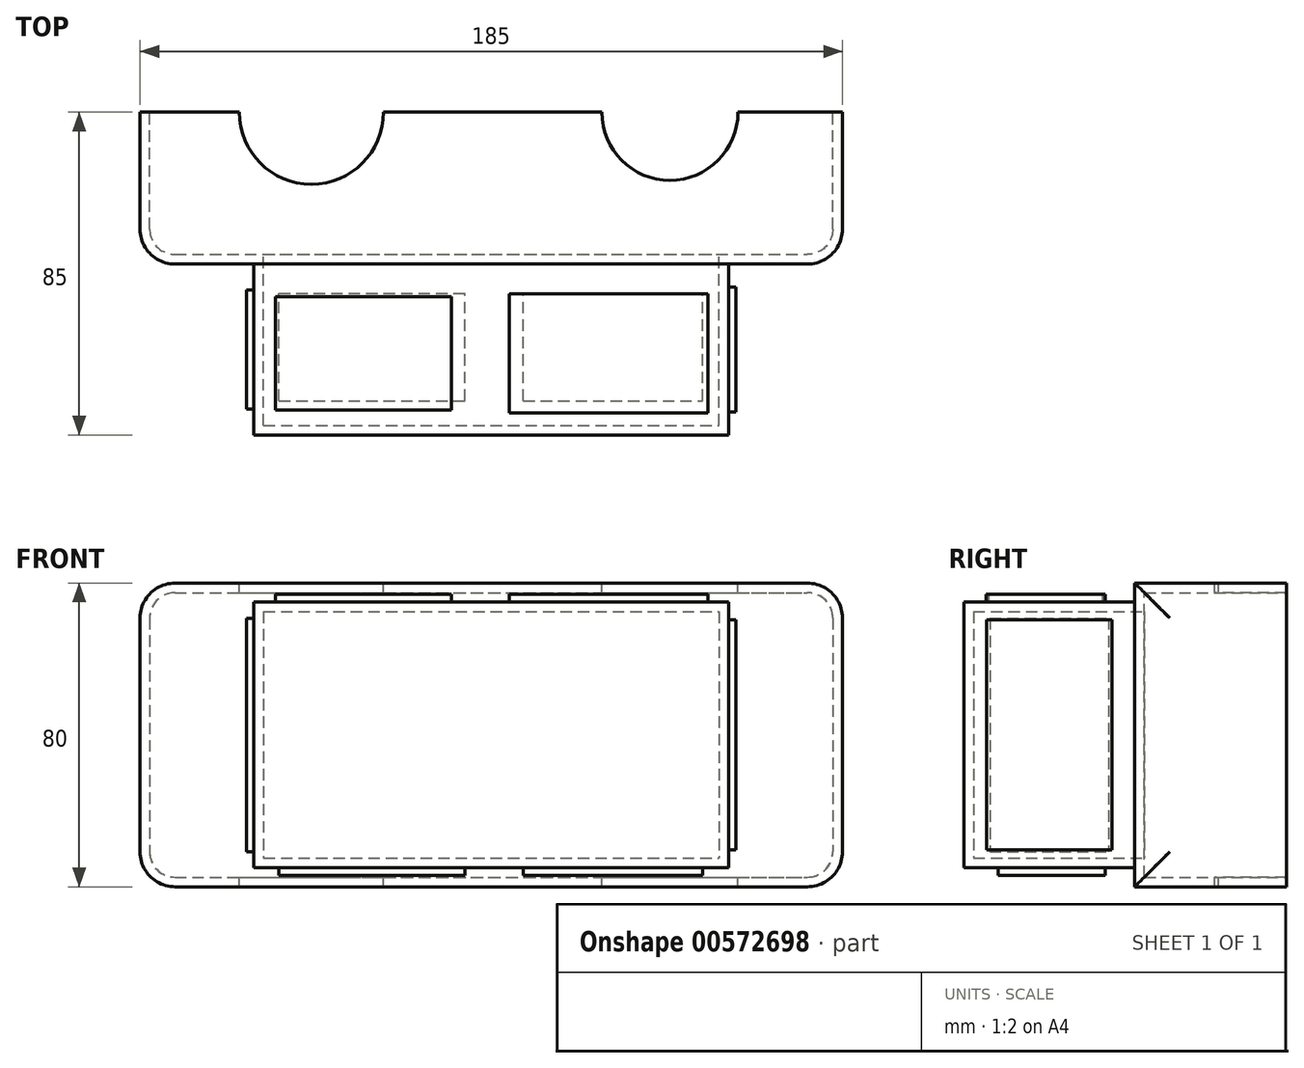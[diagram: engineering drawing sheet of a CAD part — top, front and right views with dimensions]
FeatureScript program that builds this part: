
annotation { "Feature Type Name" : "Feature", "Feature Type Description" : "" }
export const myFeature = defineFeature(function(context is Context, id is Id, definition is map)
    precondition{}
    {
        {
            var Q0;
            Q0=qCreatedBy(makeId("Front.planeOp"),FACE);
            var sketch = newSketch(context, id + "F0", { "sketchPlane" : qUnion([Q0])});
            skLineSegment(sketch, "E0.bottom", {"start": v(-92.5, 40) * mm, "end": v(92.5, 40) * mm});
            skLineSegment(sketch, "E0.top", {"start": v(-92.5, -40) * mm, "end": v(92.5, -40) * mm});
            skLineSegment(sketch, "E0.left", {"start": v(-92.5, 40) * mm, "end": v(-92.5, -40) * mm});
            skLineSegment(sketch, "E0.right", {"start": v(92.5, 40) * mm, "end": v(92.5, -40) * mm});
            skPoint(sketch, "E0.middle", {"position": v(0, 0) * mm});
            skSolve(sketch);
        }
        {
            var Q0;
            Q0=makeQuery(id+"F0.imprint","IMPRINT",FACE,{"disambiguationData":[TD([[makeQuery(id+"F0.imprint","IMPRINT",EDGE,{"derivedFrom":sQuery(id+"F0.wireOp",EDGE,"E0.bottom")}),-1.0]])]});
            extrude(context, id + "F1", {"entities" : qUnion([Q0]), "depth" : 40 * mm, "offsetDistance" : 25.4 * mm});
        }
        {
            var Q0;
            Q0=makeQuery(id+"F1.opExtrude","CAP_FACE",FACE,{"disambiguationData":[OSD([sQuery(id+"F0.wireOp",EDGE,"E0.bottom"),sQuery(id+"F0.wireOp",EDGE,"E0.top"),sQuery(id+"F0.wireOp",EDGE,"E0.left"),sQuery(id+"F0.wireOp",EDGE,"E0.right")])],"isStart":false});
            var sketch = newSketch(context, id + "F2", { "sketchPlane" : qUnion([Q0])});
            skLineSegment(sketch, "E1.bottom", {"start": v(-62.5, 35) * mm, "end": v(62.5, 35) * mm});
            skLineSegment(sketch, "E1.top", {"start": v(-62.5, -35) * mm, "end": v(62.5, -35) * mm});
            skLineSegment(sketch, "E1.left", {"start": v(-62.5, 35) * mm, "end": v(-62.5, -35) * mm});
            skLineSegment(sketch, "E1.right", {"start": v(62.5, 35) * mm, "end": v(62.5, -35) * mm});
            skPoint(sketch, "E1.middle", {"position": v(0, 0) * mm});
            skSolve(sketch);
        }
        {
            var Q0;
            Q0=makeQuery(id+"F2.imprint","IMPRINT",FACE,{"disambiguationData":[TD([[makeQuery(id+"F2.imprint","IMPRINT",EDGE,{"derivedFrom":sQuery(id+"F2.wireOp",EDGE,"E1.bottom")}),-1.0]])]});
            extrude(context, id + "F3", {"entities" : qUnion([Q0]), "operationType" : NewBodyOperationType.ADD, "depth" : 45 * mm, "offsetDistance" : 25.4 * mm});
        }
        {
            var Q0;
            Q0=makeQuery(id+"F1.opExtrude","CAP_EDGE",EDGE,{"disambiguationData":[OSD([sQuery(id+"F0.wireOp",EDGE,"E0.left")])],"isStart":false});
            var Q1;
            Q1=makeQuery(id+"F1.opExtrude","CAP_EDGE",EDGE,{"disambiguationData":[OSD([sQuery(id+"F0.wireOp",EDGE,"E0.right")])],"isStart":false});
            var Q2;
            Q2=makeQuery(id+"F1.opExtrude","SWEPT_EDGE",EDGE,{"disambiguationData":[OSD([sQuery(id+"F0.wireOp",EDGE,"E0.bottom"),sQuery(id+"F0.wireOp",EDGE,"E0.right")])]});
            var Q3;
            Q3=makeQuery(id+"F1.opExtrude","SWEPT_EDGE",EDGE,{"disambiguationData":[OSD([sQuery(id+"F0.wireOp",EDGE,"E0.top"),sQuery(id+"F0.wireOp",EDGE,"E0.right")])]});
            var Q4;
            Q4=makeQuery(id+"F1.opExtrude","SWEPT_EDGE",EDGE,{"disambiguationData":[OSD([sQuery(id+"F0.wireOp",EDGE,"E0.top"),sQuery(id+"F0.wireOp",EDGE,"E0.left")])]});
            var Q5;
            Q5=makeQuery(id+"F1.opExtrude","SWEPT_EDGE",EDGE,{"disambiguationData":[OSD([sQuery(id+"F0.wireOp",EDGE,"E0.bottom"),sQuery(id+"F0.wireOp",EDGE,"E0.left")])]});
            fillet(context, id + "F4", {"entities" : qUnion([Q0, Q1, Q2, Q3, Q4, Q5]), "radius" : 9.2 * mm, "tangentPropagation" : true, "allowEdgeOverflow" : false});
        }
        {
            var Q0;
            Q0=makeQuery(id+"F1.opExtrude","CAP_FACE",FACE,{"disambiguationData":[OSD([sQuery(id+"F0.wireOp",EDGE,"E0.bottom"),sQuery(id+"F0.wireOp",EDGE,"E0.top"),sQuery(id+"F0.wireOp",EDGE,"E0.left"),sQuery(id+"F0.wireOp",EDGE,"E0.right")])],"isStart":true});
            shell(context, id + "F5", {"entities" : qUnion([Q0]), "thickness" : 2.54 * mm});
        }
        {
            var Q0;
            Q0=makeQuery(id+"F1.opExtrude","SWEPT_FACE",FACE,{"disambiguationData":[OSD([sQuery(id+"F0.wireOp",EDGE,"E0.bottom")])]});
            var sketch = newSketch(context, id + "F6", { "sketchPlane" : qUnion([Q0])});
            skCircle(sketch, "E2", {"center": v(-47.36, 0) * mm, "radius": 18.99 * mm});
            skCircle(sketch, "E3", {"center": v(47.06, 0) * mm, "radius": 17.94 * mm});
            skSolve(sketch);
        }
        {
            var Q0;
            {var subQ0=sQuery(id+"F6.wireOp",EDGE,"E2");var subQ1=makeQuery(id+"F1.opExtrude","CAP_EDGE",EDGE,{"disambiguationData":[OSD([sQuery(id+"F0.wireOp",EDGE,"E0.bottom")])],"isStart":true});var subQ2=makeQuery(id+"F6.imprint","INTERSECT",VERTEX,{"disambiguationData":[OD(0.0)],"derivedFrom":[subQ1,subQ0]});Q0=makeQuery(id+"F6.imprint","IMPRINT",FACE,{"disambiguationData":[TD([[makeQuery(id+"F6.imprint","IMPRINT",EDGE,{"disambiguationData":[TD([[subQ2,-1.0]])],"derivedFrom":subQ0}),1.0]])]});}
            var Q1;
            {var subQ0=sQuery(id+"F6.wireOp",EDGE,"E3");var subQ1=makeQuery(id+"F1.opExtrude","CAP_EDGE",EDGE,{"disambiguationData":[OSD([sQuery(id+"F0.wireOp",EDGE,"E0.bottom")])],"isStart":true});var subQ2=makeQuery(id+"F6.imprint","INTERSECT",VERTEX,{"disambiguationData":[OD(0.0)],"derivedFrom":[subQ1,subQ0]});Q1=makeQuery(id+"F6.imprint","IMPRINT",FACE,{"disambiguationData":[TD([[makeQuery(id+"F6.imprint","IMPRINT",EDGE,{"disambiguationData":[TD([[subQ2,1.0]])],"derivedFrom":subQ0}),1.0]])]});}
            extrude(context, id + "F7", {"entities" : qUnion([Q0, Q1]), "operationType" : NewBodyOperationType.REMOVE, "oppositeDirection" : true, "depth" : 112.6 * mm, "offsetDistance" : 25 * mm});
        }
        {
            var Q0;
            Q0=makeQuery(id+"F3.opExtrude","SWEPT_FACE",FACE,{"disambiguationData":[OSD([sQuery(id+"F2.wireOp",EDGE,"E1.top")])]});
            var sketch = newSketch(context, id + "F8", { "sketchPlane" : qUnion([Q0])});
            skLineSegment(sketch, "E4.bottom", {"start": v(-55.95, 75.97) * mm, "end": v(-6.9, 75.97) * mm});
            skLineSegment(sketch, "E4.top", {"start": v(-55.95, 47.77) * mm, "end": v(-6.9, 47.77) * mm});
            skLineSegment(sketch, "E4.left", {"start": v(-55.95, 75.97) * mm, "end": v(-55.95, 47.77) * mm});
            skLineSegment(sketch, "E4.right", {"start": v(-6.9, 75.97) * mm, "end": v(-6.9, 47.77) * mm});
            skPoint(sketch, "E4.middle", {"position": v(-31.42, 61.87) * mm});
            skLineSegment(sketch, "E5.bottom", {"start": v(8.43, 75.97) * mm, "end": v(55.64, 75.97) * mm});
            skLineSegment(sketch, "E5.top", {"start": v(8.43, 47.77) * mm, "end": v(55.64, 47.77) * mm});
            skLineSegment(sketch, "E5.left", {"start": v(8.43, 75.97) * mm, "end": v(8.43, 47.77) * mm});
            skLineSegment(sketch, "E5.right", {"start": v(55.64, 75.97) * mm, "end": v(55.64, 47.77) * mm});
            skPoint(sketch, "E5.middle", {"position": v(32.04, 61.87) * mm});
            skSolve(sketch);
        }
        {
            var Q0;
            Q0=makeQuery(id+"F8.imprint","IMPRINT",FACE,{"disambiguationData":[TD([[makeQuery(id+"F8.imprint","IMPRINT",EDGE,{"derivedFrom":sQuery(id+"F8.wireOp",EDGE,"E4.bottom")}),-1.0]])]});
            var Q1;
            Q1=makeQuery(id+"F8.imprint","IMPRINT",FACE,{"disambiguationData":[TD([[makeQuery(id+"F8.imprint","IMPRINT",EDGE,{"derivedFrom":sQuery(id+"F8.wireOp",EDGE,"E5.bottom")}),-1.0]])]});
            extrude(context, id + "F9", {"entities" : qUnion([Q0, Q1]), "operationType" : NewBodyOperationType.ADD, "depth" : 2 * mm, "offsetDistance" : 25 * mm});
        }
        {
            var Q0;
            Q0=makeQuery(id+"F3.opExtrude","SWEPT_FACE",FACE,{"disambiguationData":[OSD([sQuery(id+"F2.wireOp",EDGE,"E1.bottom")])]});
            var sketch = newSketch(context, id + "F10", { "sketchPlane" : qUnion([Q0])});
            skLineSegment(sketch, "E6.bottom", {"start": v(57.04, -79.2) * mm, "end": v(4.8, -79.2) * mm});
            skLineSegment(sketch, "E6.top", {"start": v(57.04, -47.82) * mm, "end": v(4.8, -47.82) * mm});
            skLineSegment(sketch, "E6.left", {"start": v(57.04, -79.2) * mm, "end": v(57.04, -47.82) * mm});
            skLineSegment(sketch, "E6.right", {"start": v(4.8, -79.2) * mm, "end": v(4.8, -47.82) * mm});
            skPoint(sketch, "E6.middle", {"position": v(30.92, -63.5) * mm});
            skLineSegment(sketch, "E7.bottom", {"start": v(-10.53, -78.47) * mm, "end": v(-56.86, -78.47) * mm});
            skLineSegment(sketch, "E7.top", {"start": v(-10.53, -48.54) * mm, "end": v(-56.86, -48.54) * mm});
            skLineSegment(sketch, "E7.left", {"start": v(-10.53, -78.47) * mm, "end": v(-10.53, -48.54) * mm});
            skLineSegment(sketch, "E7.right", {"start": v(-56.86, -78.47) * mm, "end": v(-56.86, -48.54) * mm});
            skPoint(sketch, "E7.middle", {"position": v(-33.7, -63.5) * mm});
            skPoint(sketch, "E7.middle.positionSnap0", {"position": v(4.8, -63.5) * mm});
            skPoint(sketch, "E7.centerSnap0", {"position": v(4.8, -63.5) * mm});
            skSolve(sketch);
        }
        {
            var Q0;
            Q0=makeQuery(id+"F10.imprint","IMPRINT",FACE,{"disambiguationData":[TD([[makeQuery(id+"F10.imprint","IMPRINT",EDGE,{"derivedFrom":sQuery(id+"F10.wireOp",EDGE,"E6.bottom")}),-1.0]])]});
            var Q1;
            Q1=makeQuery(id+"F10.imprint","IMPRINT",FACE,{"disambiguationData":[TD([[makeQuery(id+"F10.imprint","IMPRINT",EDGE,{"derivedFrom":sQuery(id+"F10.wireOp",EDGE,"E7.bottom")}),-1.0]])]});
            extrude(context, id + "F11", {"entities" : qUnion([Q0, Q1]), "operationType" : NewBodyOperationType.ADD, "depth" : 2 * mm, "offsetDistance" : 25 * mm});
        }
        {
            var Q0;
            Q0=makeQuery(id+"F3.opExtrude","SWEPT_FACE",FACE,{"disambiguationData":[OSD([sQuery(id+"F2.wireOp",EDGE,"E1.left")])]});
            var sketch = newSketch(context, id + "F12", { "sketchPlane" : qUnion([Q0])});
            skLineSegment(sketch, "E8.bottom", {"start": v(78.17, 30.74) * mm, "end": v(46.83, 30.74) * mm});
            skLineSegment(sketch, "E8.top", {"start": v(78.17, -30.74) * mm, "end": v(46.83, -30.74) * mm});
            skLineSegment(sketch, "E8.left", {"start": v(78.17, 30.74) * mm, "end": v(78.17, -30.74) * mm});
            skLineSegment(sketch, "E8.right", {"start": v(46.83, 30.74) * mm, "end": v(46.83, -30.74) * mm});
            skPoint(sketch, "E8.middle", {"position": v(62.5, 0) * mm});
            skPoint(sketch, "E8.middle.positionSnap0", {"position": v(62.5, 35) * mm});
            skPoint(sketch, "E8.centerSnap0", {"position": v(62.5, 35) * mm});
            skSolve(sketch);
        }
        {
            var Q0;
            Q0=makeQuery(id+"F12.imprint","IMPRINT",FACE,{"disambiguationData":[TD([[makeQuery(id+"F12.imprint","IMPRINT",EDGE,{"derivedFrom":sQuery(id+"F12.wireOp",EDGE,"E8.bottom")}),1.0]])]});
            extrude(context, id + "F13", {"entities" : qUnion([Q0]), "operationType" : NewBodyOperationType.ADD, "depth" : 2 * mm, "offsetDistance" : 25 * mm});
        }
        {
            var Q0;
            Q0=makeQuery(id+"F3.opExtrude","SWEPT_FACE",FACE,{"disambiguationData":[OSD([sQuery(id+"F2.wireOp",EDGE,"E1.right")])]});
            var sketch = newSketch(context, id + "F14", { "sketchPlane" : qUnion([Q0])});
            skLineSegment(sketch, "E9.bottom", {"start": v(-79, 30.32) * mm, "end": v(-46, 30.32) * mm});
            skLineSegment(sketch, "E9.top", {"start": v(-79, -30.32) * mm, "end": v(-46, -30.32) * mm});
            skLineSegment(sketch, "E9.left", {"start": v(-79, 30.32) * mm, "end": v(-79, -30.32) * mm});
            skLineSegment(sketch, "E9.right", {"start": v(-46, 30.32) * mm, "end": v(-46, -30.32) * mm});
            skPoint(sketch, "E9.middle", {"position": v(-62.5, 0) * mm});
            skPoint(sketch, "E9.middle.positionSnap0", {"position": v(-62.5, 35) * mm});
            skPoint(sketch, "E9.centerSnap0", {"position": v(-62.5, 35) * mm});
            skSolve(sketch);
        }
        {
            var Q0;
            Q0=makeQuery(id+"F14.imprint","IMPRINT",FACE,{"disambiguationData":[TD([[makeQuery(id+"F14.imprint","IMPRINT",EDGE,{"derivedFrom":sQuery(id+"F14.wireOp",EDGE,"E9.bottom")}),-1.0]])]});
            extrude(context, id + "F15", {"entities" : qUnion([Q0]), "operationType" : NewBodyOperationType.ADD, "depth" : 2 * mm, "offsetDistance" : 25 * mm});
        }
    });
